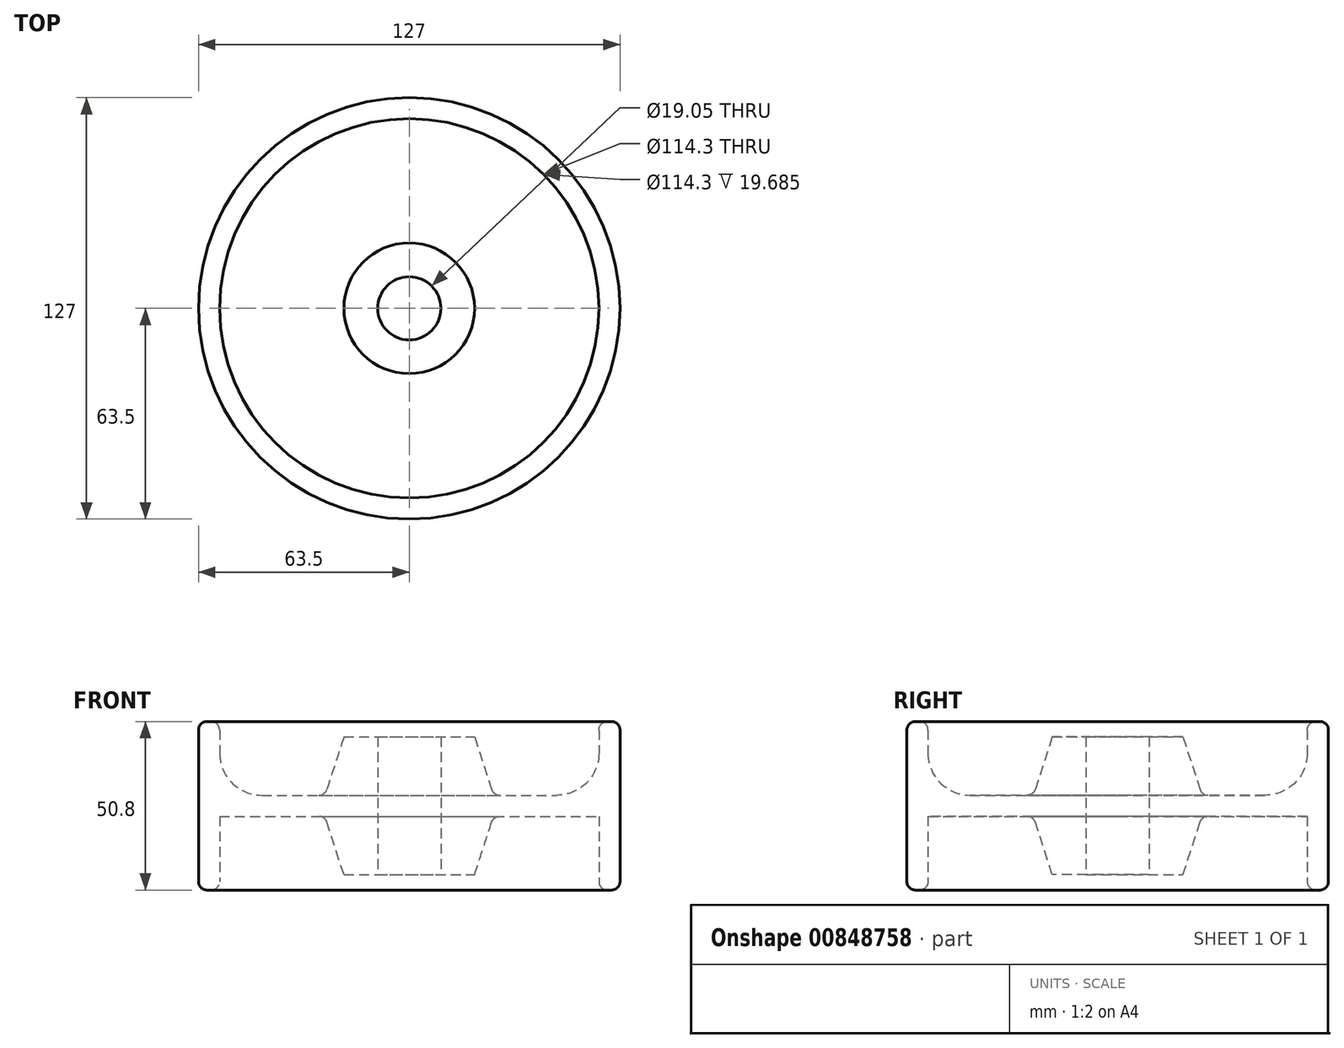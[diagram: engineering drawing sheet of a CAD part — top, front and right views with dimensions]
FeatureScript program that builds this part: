
annotation { "Feature Type Name" : "Feature", "Feature Type Description" : "" }
export const myFeature = defineFeature(function(context is Context, id is Id, definition is map)
    precondition{}
    {
        {
            var Q0;
            Q0=qCreatedBy(makeId("Front.planeOp"),FACE);
            var sketch = newSketch(context, id + "F0", { "sketchPlane" : qUnion([Q0])});
            skLineSegment(sketch, "E0", {"start": v(0, 0) * mm, "end": v(0, 56.62) * mm, "construction": true});
            skLineSegment(sketch, "E1", {"start": v(0, 0) * mm, "end": v(-82.25, 0) * mm, "construction": true});
            skLineSegment(sketch, "E2", {"start": v(-9.53, 0) * mm, "end": v(-9.53, 20.76) * mm});
            skLineSegment(sketch, "E3", {"start": v(-9.52, 20.76) * mm, "end": v(-19.69, 20.76) * mm});
            skLineSegment(sketch, "E4", {"start": v(-19.69, 20.76) * mm, "end": v(-25.4, 3.17) * mm});
            skLineSegment(sketch, "E5", {"start": v(-25.4, 3.18) * mm, "end": v(-57.15, 3.17) * mm});
            skLineSegment(sketch, "E6", {"start": v(-57.15, 3.18) * mm, "end": v(-57.15, 25.4) * mm});
            skLineSegment(sketch, "E7", {"start": v(-57.15, 25.4) * mm, "end": v(-63.5, 25.4) * mm});
            skLineSegment(sketch, "E8", {"start": v(-63.5, 25.4) * mm, "end": v(-63.5, 0) * mm});
            skLineSegment(sketch, "E9.MirrorCS", {"start": v(-63.5, -25.4) * mm, "end": v(-63.5, 0) * mm});
            skLineSegment(sketch, "E10.MirrorCS", {"start": v(-9.52, -20.76) * mm, "end": v(-19.68, -20.76) * mm});
            skLineSegment(sketch, "E11.MirrorCS", {"start": v(-9.53, 0) * mm, "end": v(-9.52, -20.76) * mm});
            skLineSegment(sketch, "E12.MirrorCS", {"start": v(-19.68, -20.76) * mm, "end": v(-25.4, -3.17) * mm});
            skLineSegment(sketch, "E13.MirrorCS", {"start": v(-57.15, -25.4) * mm, "end": v(-63.5, -25.4) * mm});
            skLineSegment(sketch, "E14.MirrorCS", {"start": v(-57.15, -3.18) * mm, "end": v(-57.15, -25.4) * mm});
            skLineSegment(sketch, "E15.MirrorCS", {"start": v(-25.4, -3.17) * mm, "end": v(-57.15, -3.18) * mm});
            skSolve(sketch);
        }
        {
            var Q0;
            Q0 = qSketchRegion(id + "F0", true);
            var Q1;
            Q1=sQuery(id+"F0.wireOp",EDGE,"E0");
            revolve(context, id + "F1", {"surfaceOperationType" : NewSurfaceOperationType.NEW, "entities" : qUnion([Q0]), "axis" : qUnion([Q1]), "revolveType" : RevolveType.FULL});
        }
        {
            var Q0;
            Q0=makeQuery(id+"F1.opRevolve","SWEPT_EDGE",EDGE,{"disambiguationData":[OSD([sQuery(id+"F0.wireOp",EDGE,"E7"),sQuery(id+"F0.wireOp",EDGE,"E8")])]});
            var Q1;
            Q1=makeQuery(id+"F1.opRevolve","SWEPT_EDGE",EDGE,{"disambiguationData":[OSD([sQuery(id+"F0.wireOp",EDGE,"E13.MirrorCS"),sQuery(id+"F0.wireOp",EDGE,"E14.MirrorCS")])]});
            var Q2;
            Q2=makeQuery(id+"F1.opRevolve","SWEPT_EDGE",EDGE,{"disambiguationData":[OSD([sQuery(id+"F0.wireOp",EDGE,"E6"),sQuery(id+"F0.wireOp",EDGE,"E7")])]});
            var Q3;
            Q3=makeQuery(id+"F1.opRevolve","SWEPT_EDGE",EDGE,{"disambiguationData":[OSD([sQuery(id+"F0.wireOp",EDGE,"E9.MirrorCS"),sQuery(id+"F0.wireOp",EDGE,"E13.MirrorCS")])]});
            var Q4;
            Q4=makeQuery(id+"F1.opRevolve","SWEPT_EDGE",EDGE,{"disambiguationData":[OSD([sQuery(id+"F0.wireOp",EDGE,"E12.MirrorCS"),sQuery(id+"F0.wireOp",EDGE,"E15.MirrorCS")])]});
            var Q5;
            Q5=makeQuery(id+"F1.opRevolve","SWEPT_EDGE",EDGE,{"disambiguationData":[OSD([sQuery(id+"F0.wireOp",EDGE,"E4"),sQuery(id+"F0.wireOp",EDGE,"E5")])]});
            fillet(context, id + "F2", {"entities" : qUnion([Q0, Q1, Q2, Q3, Q4, Q5]), "radius" : 2.54 * mm, "tangentPropagation" : true, "allowEdgeOverflow" : false});
        }
        {
            var Q0;
            Q0=makeQuery(id+"F1.opRevolve","SWEPT_EDGE",EDGE,{"disambiguationData":[OSD([sQuery(id+"F0.wireOp",EDGE,"E5"),sQuery(id+"F0.wireOp",EDGE,"E6")])]});
            fillet(context, id + "F3", {"entities" : qUnion([Q0]), "radius" : 12.7 * mm, "tangentPropagation" : true, "allowEdgeOverflow" : false});
        }
    });
